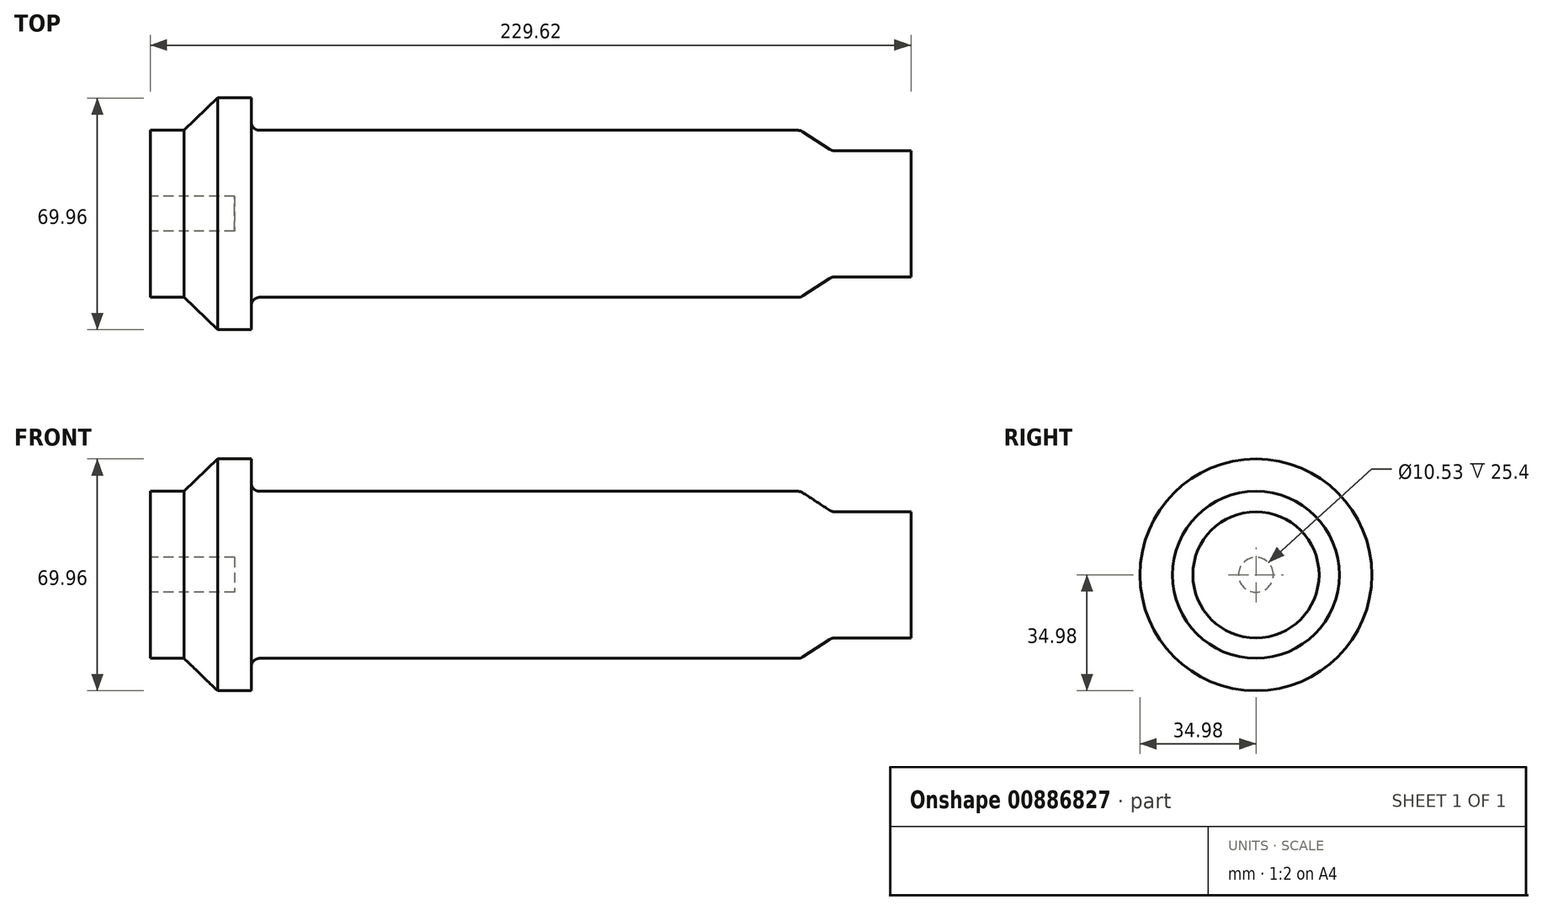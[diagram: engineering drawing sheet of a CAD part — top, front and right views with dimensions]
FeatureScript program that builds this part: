
annotation { "Feature Type Name" : "Feature", "Feature Type Description" : "" }
export const myFeature = defineFeature(function(context is Context, id is Id, definition is map)
    precondition{}
    {
        {
            var Q0;
            Q0=qCreatedBy(makeId("Front.planeOp"),FACE);
            var sketch = newSketch(context, id + "F0", { "sketchPlane" : qUnion([Q0])});
            skLineSegment(sketch, "E0", {"start": v(0, 0) * mm, "end": v(0, 19.05) * mm});
            skLineSegment(sketch, "E1", {"start": v(0, 19.05) * mm, "end": v(-23.88, 19.05) * mm});
            skLineSegment(sketch, "E2", {"start": v(-23.88, 19.05) * mm, "end": v(-33.31, 25.2) * mm});
            skLineSegment(sketch, "E3", {"start": v(-33.31, 25.2) * mm, "end": v(-199.14, 25.2) * mm});
            skLineSegment(sketch, "E4", {"start": v(-199.14, 25.2) * mm, "end": v(-199.14, 34.98) * mm});
            skLineSegment(sketch, "E5", {"start": v(-199.14, 34.98) * mm, "end": v(-209.3, 34.98) * mm});
            skLineSegment(sketch, "E6", {"start": v(0, 0) * mm, "end": v(-229.62, 0) * mm});
            skLineSegment(sketch, "E7", {"start": v(-229.62, 25.2) * mm, "end": v(-229.62, 0) * mm});
            skLineSegment(sketch, "E8", {"start": v(-229.62, 25.2) * mm, "end": v(-219.46, 25.2) * mm});
            skLineSegment(sketch, "E9", {"start": v(-219.46, 25.2) * mm, "end": v(-209.3, 34.98) * mm});
            skLineSegment(sketch, "E10", {"start": v(-199.14, 25.2) * mm, "end": v(-219.46, 25.2) * mm, "construction": true});
            skSolve(sketch);
        }
        {
            var Q0;
            Q0=makeQuery(id+"F0.imprint","IMPRINT",FACE,{"disambiguationData":[TD([[makeQuery(id+"F0.imprint","IMPRINT",EDGE,{"derivedFrom":sQuery(id+"F0.wireOp",EDGE,"E0")}),1.0]])]});
            var Q1;
            Q1=sQuery(id+"F0.wireOp",EDGE,"E6");
            revolve(context, id + "F1", {"surfaceOperationType" : NewSurfaceOperationType.NEW, "entities" : qUnion([Q0]), "axis" : qUnion([Q1]), "revolveType" : RevolveType.FULL});
        }
        {
            var Q0;
            Q0=makeQuery(id+"F1.opRevolve","SWEPT_FACE",FACE,{"disambiguationData":[OSD([sQuery(id+"F0.wireOp",EDGE,"E7")])]});
            var sketch = newSketch(context, id + "F2", { "sketchPlane" : qUnion([Q0])});
            skCircle(sketch, "E11", {"center": v(0, 0) * mm, "radius": 5.26 * mm});
            skSolve(sketch);
        }
        {
            var Q0;
            Q0=makeQuery(id+"F2.imprint","IMPRINT",FACE,{"disambiguationData":[TD([[makeQuery(id+"F2.imprint","IMPRINT",EDGE,{"derivedFrom":sQuery(id+"F2.wireOp",EDGE,"E11")}),1.0]])]});
            extrude(context, id + "F3", {"entities" : qUnion([Q0]), "operationType" : NewBodyOperationType.REMOVE, "oppositeDirection" : true, "depth" : 25.4 * mm, "offsetDistance" : 25.4 * mm});
        }
        {
            var Q0;
            Q0=makeQuery(id+"F1.opRevolve","SWEPT_FACE",FACE,{"disambiguationData":[OSD([sQuery(id+"F0.wireOp",EDGE,"E0")])]});
            var sketch = newSketch(context, id + "F4", { "sketchPlane" : qUnion([Q0])});
            skCircle(sketch, "E12", {"center": v(0, 0) * mm, "radius": 2.38 * mm});
            skSolve(sketch);
        }
        {
            var Q0;
            Q0=makeQuery(id+"F1.opRevolve","SWEPT_EDGE",EDGE,{"disambiguationData":[OSD([sQuery(id+"F0.wireOp",EDGE,"E1"),sQuery(id+"F0.wireOp",EDGE,"E2")])]});
            var Q1;
            Q1=makeQuery(id+"F1.opRevolve","SWEPT_EDGE",EDGE,{"disambiguationData":[OSD([sQuery(id+"F0.wireOp",EDGE,"E2"),sQuery(id+"F0.wireOp",EDGE,"E3")])]});
            fillet(context, id + "F5", {"entities" : qUnion([Q0, Q1]), "radius" : 2.54 * mm, "tangentPropagation" : true, "allowEdgeOverflow" : false});
        }
        {
            var Q0;
            Q0=makeQuery(id+"F1.opRevolve","SWEPT_EDGE",EDGE,{"disambiguationData":[OSD([sQuery(id+"F0.wireOp",EDGE,"E3"),sQuery(id+"F0.wireOp",EDGE,"E4")])]});
            fillet(context, id + "F6", {"entities" : qUnion([Q0]), "radius" : 2.54 * mm, "tangentPropagation" : true, "allowEdgeOverflow" : false});
        }
    });
